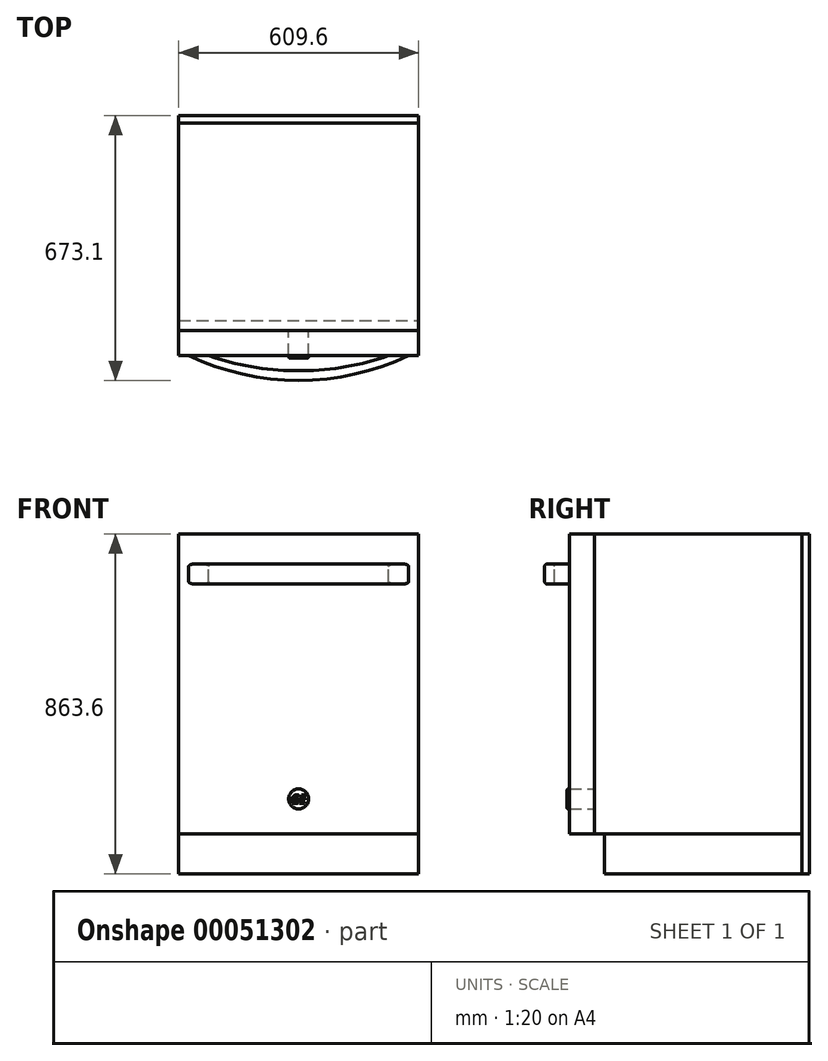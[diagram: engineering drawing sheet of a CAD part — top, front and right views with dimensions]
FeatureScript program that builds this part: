
annotation { "Feature Type Name" : "Feature", "Feature Type Description" : "" }
export const myFeature = defineFeature(function(context is Context, id is Id, definition is map)
    precondition{}
    {
        {
            var Q0;
            Q0=qCreatedBy(makeId("Front.planeOp"),FACE);
            var sketch = newSketch(context, id + "F0", { "sketchPlane" : qUnion([Q0])});
            skLineSegment(sketch, "E0.bottom", {"start": v(-304.8, 431.8) * mm, "end": v(304.8, 431.8) * mm});
            skLineSegment(sketch, "E0.top", {"start": v(-304.8, -431.8) * mm, "end": v(304.8, -431.8) * mm});
            skLineSegment(sketch, "E0.left", {"start": v(-304.8, 431.8) * mm, "end": v(-304.8, -431.8) * mm});
            skLineSegment(sketch, "E0.right", {"start": v(304.8, 431.8) * mm, "end": v(304.8, -431.8) * mm});
            skLineSegment(sketch, "E1", {"start": v(-304.8, 431.8) * mm, "end": v(304.8, -431.8) * mm, "construction": true});
            skLineSegment(sketch, "E2.bottom", {"start": v(-304.8, -330.2) * mm, "end": v(304.8, -330.2) * mm});
            skLineSegment(sketch, "E2.left", {"start": v(-304.8, -330.2) * mm, "end": v(-304.8, 431.8) * mm});
            skLineSegment(sketch, "E2.right", {"start": v(304.8, -330.2) * mm, "end": v(304.8, 431.8) * mm});
            skLineSegment(sketch, "E3", {"start": v(0, 0) * mm, "end": v(0, -330.2) * mm, "construction": true});
            skCircle(sketch, "E4", {"center": v(0, -241.3) * mm, "radius": 25.4 * mm});
            skLineSegment(sketch, "E5.bottom", {"start": v(-279.4, 355.6) * mm, "end": v(279.4, 355.6) * mm});
            skLineSegment(sketch, "E5.top", {"start": v(-279.4, 304.8) * mm, "end": v(279.4, 304.8) * mm});
            skLineSegment(sketch, "E5.left", {"start": v(-279.4, 355.6) * mm, "end": v(-279.4, 304.8) * mm});
            skLineSegment(sketch, "E5.right", {"start": v(279.4, 355.6) * mm, "end": v(279.4, 304.8) * mm});
            skLineSegment(sketch, "E6", {"start": v(0, 431.8) * mm, "end": v(0, 304.8) * mm, "construction": true});
            skSolve(sketch);
        }
        {
            var Q0;
            Q0=makeQuery(id+"F0.imprint","IMPRINT",FACE,{"disambiguationData":[TD([[makeQuery(id+"F0.imprint","IMPRINT",EDGE,{"derivedFrom":sQuery(id+"F0.wireOp",EDGE,"E2.bottom")}),1.0]])]});
            var Q1;
            Q1=makeQuery(id+"F0.imprint","IMPRINT",FACE,{"disambiguationData":[TD([[makeQuery(id+"F0.imprint","IMPRINT",EDGE,{"derivedFrom":sQuery(id+"F0.wireOp",EDGE,"E5.bottom")}),-1.0]])]});
            var Q2;
            Q2=makeQuery(id+"F0.imprint","IMPRINT",FACE,{"disambiguationData":[TD([[makeQuery(id+"F0.imprint","IMPRINT",EDGE,{"derivedFrom":sQuery(id+"F0.wireOp",EDGE,"E4")}),1.0]])]});
            var Q3;
            Q3=sQuery(id+"F0.wireOp",EDGE,"E2.right");
            var Q4;
            Q4=sQuery(id+"F0.wireOp",EDGE,"E0.bottom");
            var Q5;
            Q5=sQuery(id+"F0.wireOp",EDGE,"E2.left");
            var Q6;
            Q6=sQuery(id+"F0.wireOp",EDGE,"E2.bottom");
            extrude(context, id + "F1", {"entities" : qUnion([Q0, Q1, Q2]), "surfaceEntities" : qUnion([Q3, Q4, Q5, Q6]), "depth" : 63.5 * mm});
        }
        {
            var Q0;
            Q0=makeQuery(id+"F0.imprint","IMPRINT",FACE,{"disambiguationData":[TD([[makeQuery(id+"F0.imprint","IMPRINT",EDGE,{"derivedFrom":sQuery(id+"F0.wireOp",EDGE,"E0.top")}),1.0]])]});
            extrude(context, id + "F2", {"entities" : qUnion([Q0]), "oppositeDirection" : true, "depth" : 527.05 * mm});
        }
        {
            var Q0;
            Q0=makeQuery(id+"F0.imprint","IMPRINT",FACE,{"disambiguationData":[TD([[makeQuery(id+"F0.imprint","IMPRINT",EDGE,{"derivedFrom":sQuery(id+"F0.wireOp",EDGE,"E5.bottom")}),-1.0]])]});
            extrude(context, id + "F3", {"entities" : qUnion([Q0]), "operationType" : NewBodyOperationType.ADD, "depth" : 127 * mm});
        }
        {
            var Q0;
            Q0=makeQuery(id+"F3.opExtrude","SWEPT_FACE",FACE,{"disambiguationData":[OSD([sQuery(id+"F0.wireOp",EDGE,"E5.bottom")])]});
            var sketch = newSketch(context, id + "F4", { "sketchPlane" : qUnion([Q0])});
            skLineSegment(sketch, "E7.bottom", {"start": v(-228.6, -63.5) * mm, "end": v(228.6, -63.5) * mm});
            skLineSegment(sketch, "E7.top", {"start": v(-228.6, -101.6) * mm, "end": v(228.6, -101.6) * mm});
            skLineSegment(sketch, "E7.left", {"start": v(-228.6, -63.5) * mm, "end": v(-228.6, -101.6) * mm});
            skLineSegment(sketch, "E7.right", {"start": v(228.6, -63.5) * mm, "end": v(228.6, -101.6) * mm});
            skSolve(sketch);
        }
        {
            var Q0;
            Q0=qSketchRegion(id+"F4",true);
            extrude(context, id + "F5", {"entities" : qUnion([Q0]), "operationType" : NewBodyOperationType.REMOVE, "endBound" : BoundingType.THROUGH_ALL, "oppositeDirection" : true, "depth" : 25.4 * mm});
        }
        {
            var Q0;
            Q0=makeQuery(id+"F5.boolean.opBoolean","COPY",EDGE,{"derivedFrom":makeQuery(id+"F5.opExtrude","SWEPT_EDGE",EDGE,{"disambiguationData":[OSD([sQuery(id+"F4.wireOp",EDGE,"E7.top"),sQuery(id+"F4.wireOp",EDGE,"E7.right")])]})});
            var Q1;
            Q1=makeQuery(id+"F5.boolean.opBoolean","COPY",EDGE,{"derivedFrom":makeQuery(id+"F5.opExtrude","SWEPT_EDGE",EDGE,{"disambiguationData":[OSD([sQuery(id+"F4.wireOp",EDGE,"E7.top"),sQuery(id+"F4.wireOp",EDGE,"E7.left")])]})});
            var Q2;
            Q2=makeQuery(id+"F3.opExtrude","CAP_EDGE",EDGE,{"disambiguationData":[OSD([sQuery(id+"F0.wireOp",EDGE,"E5.left")])],"isStart":false});
            var Q3;
            Q3=makeQuery(id+"F3.opExtrude","CAP_EDGE",EDGE,{"disambiguationData":[OSD([sQuery(id+"F0.wireOp",EDGE,"E5.right")])],"isStart":false});
            fillet(context, id + "F6", {"entities" : qUnion([Q0, Q1, Q2, Q3]), "radius" : 646.43 * mm, "tangentPropagation" : true, "allowEdgeOverflow" : false});
        }
        {
            var Q0;
            Q0=makeQuery(id+"F6.opFillet","BLEND_EDGE",EDGE,{"blendedFrom":[makeQuery(id+"F3.opExtrude","CAP_EDGE",EDGE,{"disambiguationData":[OSD([sQuery(id+"F0.wireOp",EDGE,"E5.left")])],"isStart":false}),makeQuery(id+"F3.opExtrude","SWEPT_FACE",FACE,{"disambiguationData":[OSD([sQuery(id+"F0.wireOp",EDGE,"E5.bottom")])]})],"blendedInto":[makeQuery(id+"F3.opExtrude","SWEPT_FACE",FACE,{"disambiguationData":[OSD([sQuery(id+"F0.wireOp",EDGE,"E5.bottom")])]})]});
            var Q1;
            Q1=makeQuery(id+"F6.opFillet","BLEND_EDGE",EDGE,{"blendedFrom":[makeQuery(id+"F5.boolean.opBoolean","COPY",EDGE,{"derivedFrom":makeQuery(id+"F5.opExtrude","SWEPT_EDGE",EDGE,{"disambiguationData":[OSD([sQuery(id+"F4.wireOp",EDGE,"E7.top"),sQuery(id+"F4.wireOp",EDGE,"E7.right")])]})}),makeQuery(id+"F3.opExtrude","SWEPT_FACE",FACE,{"disambiguationData":[OSD([sQuery(id+"F0.wireOp",EDGE,"E5.bottom")])]})],"blendedInto":[makeQuery(id+"F3.opExtrude","SWEPT_FACE",FACE,{"disambiguationData":[OSD([sQuery(id+"F0.wireOp",EDGE,"E5.bottom")])]})]});
            var Q2;
            Q2=makeQuery(id+"F6.opFillet","BLEND_EDGE",EDGE,{"blendedFrom":[makeQuery(id+"F5.boolean.opBoolean","COPY",EDGE,{"derivedFrom":makeQuery(id+"F5.opExtrude","SWEPT_EDGE",EDGE,{"disambiguationData":[OSD([sQuery(id+"F4.wireOp",EDGE,"E7.top"),sQuery(id+"F4.wireOp",EDGE,"E7.left")])]})}),makeQuery(id+"F3.opExtrude","SWEPT_FACE",FACE,{"disambiguationData":[OSD([sQuery(id+"F0.wireOp",EDGE,"E5.bottom")])]})],"blendedInto":[makeQuery(id+"F3.opExtrude","SWEPT_FACE",FACE,{"disambiguationData":[OSD([sQuery(id+"F0.wireOp",EDGE,"E5.bottom")])]})]});
            var Q3;
            Q3=makeQuery(id+"F5.boolean.opBoolean","COPY",EDGE,{"derivedFrom":makeQuery(id+"F5.opExtrude","CAP_EDGE",EDGE,{"disambiguationData":[OSD([sQuery(id+"F4.wireOp",EDGE,"E7.top")])],"isStart":true})});
            var Q4;
            Q4=makeQuery(id+"F6.opFillet","BLEND_EDGE",EDGE,{"blendedFrom":[makeQuery(id+"F3.opExtrude","CAP_EDGE",EDGE,{"disambiguationData":[OSD([sQuery(id+"F0.wireOp",EDGE,"E5.right")])],"isStart":false}),makeQuery(id+"F3.opExtrude","SWEPT_FACE",FACE,{"disambiguationData":[OSD([sQuery(id+"F0.wireOp",EDGE,"E5.bottom")])]})],"blendedInto":[makeQuery(id+"F3.opExtrude","SWEPT_FACE",FACE,{"disambiguationData":[OSD([sQuery(id+"F0.wireOp",EDGE,"E5.bottom")])]})]});
            var Q5;
            Q5=makeQuery(id+"F6.opFillet","BLEND_EDGE",EDGE,{"blendedFrom":[makeQuery(id+"F3.opExtrude","CAP_EDGE",EDGE,{"disambiguationData":[OSD([sQuery(id+"F0.wireOp",EDGE,"E5.right")])],"isStart":false}),makeQuery(id+"F3.opExtrude","SWEPT_FACE",FACE,{"disambiguationData":[OSD([sQuery(id+"F0.wireOp",EDGE,"E5.top")])]})],"blendedInto":[makeQuery(id+"F3.opExtrude","SWEPT_FACE",FACE,{"disambiguationData":[OSD([sQuery(id+"F0.wireOp",EDGE,"E5.top")])]})]});
            var Q6;
            Q6=makeQuery(id+"F6.opFillet","BLEND_EDGE",EDGE,{"blendedFrom":[makeQuery(id+"F3.opExtrude","CAP_EDGE",EDGE,{"disambiguationData":[OSD([sQuery(id+"F0.wireOp",EDGE,"E5.left")])],"isStart":false}),makeQuery(id+"F3.opExtrude","SWEPT_FACE",FACE,{"disambiguationData":[OSD([sQuery(id+"F0.wireOp",EDGE,"E5.top")])]})],"blendedInto":[makeQuery(id+"F3.opExtrude","SWEPT_FACE",FACE,{"disambiguationData":[OSD([sQuery(id+"F0.wireOp",EDGE,"E5.top")])]})]});
            var Q7;
            Q7=makeQuery(id+"F6.opFillet","BLEND_EDGE",EDGE,{"blendedFrom":[makeQuery(id+"F5.boolean.opBoolean","COPY",EDGE,{"derivedFrom":makeQuery(id+"F5.opExtrude","SWEPT_EDGE",EDGE,{"disambiguationData":[OSD([sQuery(id+"F4.wireOp",EDGE,"E7.top"),sQuery(id+"F4.wireOp",EDGE,"E7.left")])]})}),makeQuery(id+"F3.opExtrude","SWEPT_FACE",FACE,{"disambiguationData":[OSD([sQuery(id+"F0.wireOp",EDGE,"E5.top")])]})],"blendedInto":[makeQuery(id+"F3.opExtrude","SWEPT_FACE",FACE,{"disambiguationData":[OSD([sQuery(id+"F0.wireOp",EDGE,"E5.top")])]})]});
            var Q8;
            Q8=makeQuery(id+"F6.opFillet","BLEND_EDGE",EDGE,{"blendedFrom":[makeQuery(id+"F5.boolean.opBoolean","COPY",EDGE,{"derivedFrom":makeQuery(id+"F5.opExtrude","SWEPT_EDGE",EDGE,{"disambiguationData":[OSD([sQuery(id+"F4.wireOp",EDGE,"E7.top"),sQuery(id+"F4.wireOp",EDGE,"E7.right")])]})}),makeQuery(id+"F3.opExtrude","SWEPT_FACE",FACE,{"disambiguationData":[OSD([sQuery(id+"F0.wireOp",EDGE,"E5.top")])]})],"blendedInto":[makeQuery(id+"F3.opExtrude","SWEPT_FACE",FACE,{"disambiguationData":[OSD([sQuery(id+"F0.wireOp",EDGE,"E5.top")])]})]});
            var Q9;
            Q9=makeQuery(id+"F5.boolean.opBoolean","INTERSECT",EDGE,{"derivedFrom":[makeQuery(id+"F3.opExtrude","SWEPT_FACE",FACE,{"disambiguationData":[OSD([sQuery(id+"F0.wireOp",EDGE,"E5.top")])]}),makeQuery(id+"F5.opExtrude","SWEPT_FACE",FACE,{"disambiguationData":[OSD([sQuery(id+"F4.wireOp",EDGE,"E7.top")])]})]});
            fillet(context, id + "F7", {"entities" : qUnion([Q0, Q1, Q2, Q3, Q4, Q5, Q6, Q7, Q8, Q9]), "radius" : 6.35 * mm, "tangentPropagation" : true, "allowEdgeOverflow" : false});
        }
        {
            var Q0;
            Q0=makeQuery(id+"F1.opExtrude","CAP_FACE",FACE,{"disambiguationData":[OSD([sQuery(id+"F0.wireOp",EDGE,"E2.bottom"),sQuery(id+"F0.wireOp",EDGE,"E0.bottom"),sQuery(id+"F0.wireOp",EDGE,"E2.left"),sQuery(id+"F0.wireOp",EDGE,"E2.right")])],"isStart":true});
            var Q1;
            Q1=makeQuery(id+"F2.opExtrude","CAP_FACE",FACE,{"disambiguationData":[OSD([sQuery(id+"F0.wireOp",EDGE,"E0.top"),sQuery(id+"F0.wireOp",EDGE,"E0.left"),sQuery(id+"F0.wireOp",EDGE,"E0.right"),sQuery(id+"F0.wireOp",EDGE,"E2.bottom")])],"isStart":false});
            extrude(context, id + "F8", {"entities" : qUnion([Q0]), "endBound" : BoundingType.UP_TO_SURFACE, "endBoundEntityFace" : qUnion([Q1]), "depth" : 25.4 * mm});
        }
        {
            var Q0;
            Q0=makeQuery(id+"F1.opExtrude","SWEPT_EDGE",EDGE,{"disambiguationData":[OSD([sQuery(id+"F0.wireOp",EDGE,"E0.left"),sQuery(id+"F0.wireOp",EDGE,"E2.bottom"),sQuery(id+"F0.wireOp",EDGE,"E2.left")])]});
            var Q1;
            Q1=makeQuery(id+"F1.opExtrude","SWEPT_EDGE",EDGE,{"disambiguationData":[OSD([sQuery(id+"F0.wireOp",EDGE,"E0.right"),sQuery(id+"F0.wireOp",EDGE,"E2.bottom"),sQuery(id+"F0.wireOp",EDGE,"E2.right")])]});
            fillet(context, id + "F9", {"entities" : qUnion([Q0, Q1]), "radius" : 6.35 * mm, "tangentPropagation" : true, "allowEdgeOverflow" : false});
        }
        {
            var Q0;
            Q0=makeQuery(id+"F0.imprint","IMPRINT",FACE,{"disambiguationData":[TD([[makeQuery(id+"F0.imprint","IMPRINT",EDGE,{"derivedFrom":sQuery(id+"F0.wireOp",EDGE,"E4")}),1.0]])]});
            var Q1;
            Q1=sQuery(id+"F0.wireOp",EDGE,"E4");
            extrude(context, id + "F10", {"entities" : qUnion([Q0]), "surfaceEntities" : qUnion([Q1]), "depth" : 69.85 * mm});
        }
        {
            var Q0;
            Q0=makeQuery(id+"F10.opExtrude","CAP_EDGE",EDGE,{"disambiguationData":[OSD([sQuery(id+"F0.wireOp",EDGE,"E4")])],"isStart":false});
            fillet(context, id + "F11", {"entities" : qUnion([Q0]), "radius" : 3.17 * mm, "tangentPropagation" : true, "allowEdgeOverflow" : false});
        }
        {
            var Q0;
            Q0=makeQuery(id+"F10.opExtrude","CAP_FACE",FACE,{"disambiguationData":[OSD([sQuery(id+"F0.wireOp",EDGE,"E4")])],"isStart":false});
            var sketch = newSketch(context, id + "F12", { "sketchPlane" : qUnion([Q0])});
            skText(sketch, "E8", { "text": "GE", "fontName": "OpenSans-BoldItalic.ttf"});
            const initialGuessF12  = {"E8": [-0.0191, -0.25284, 1, 0, 0.02166]};
            skSetInitialGuess(sketch, initialGuessF12);
            skSolve(sketch);
        }
        {
            var Q0;
            Q0=qSketchRegion(id+"F12",true);
            extrude(context, id + "F13", {"entities" : qUnion([Q0]), "operationType" : NewBodyOperationType.REMOVE, "oppositeDirection" : true, "depth" : 3.17 * mm});
        }
        {
            var Q0;
            Q0=makeQuery(id+"F2.opExtrude","CAP_FACE",FACE,{"disambiguationData":[OSD([sQuery(id+"F0.wireOp",EDGE,"E0.top"),sQuery(id+"F0.wireOp",EDGE,"E0.left"),sQuery(id+"F0.wireOp",EDGE,"E0.right"),sQuery(id+"F0.wireOp",EDGE,"E2.bottom")])],"isStart":true});
            extrude(context, id + "F14", {"entities" : qUnion([Q0]), "operationType" : NewBodyOperationType.REMOVE, "oppositeDirection" : true, "depth" : 25.4 * mm});
        }
        {
            var Q0;
            Q0=makeQuery(id+"F8.opExtrude","CAP_FACE",FACE,{"disambiguationData":[OSD([sQuery(id+"F0.wireOp",EDGE,"E2.bottom"),sQuery(id+"F0.wireOp",EDGE,"E0.bottom"),sQuery(id+"F0.wireOp",EDGE,"E2.left"),sQuery(id+"F0.wireOp",EDGE,"E2.right")])],"isStart":false});
            var sketch = newSketch(context, id + "F15", { "sketchPlane" : qUnion([Q0])});
            skLineSegment(sketch, "E9.bottom", {"start": v(304.8, 431.8) * mm, "end": v(-304.8, 431.8) * mm});
            skLineSegment(sketch, "E9.top", {"start": v(304.8, -431.8) * mm, "end": v(-304.8, -431.8) * mm});
            skLineSegment(sketch, "E9.left", {"start": v(304.8, 431.8) * mm, "end": v(304.8, -431.8) * mm});
            skLineSegment(sketch, "E9.right", {"start": v(-304.8, 431.8) * mm, "end": v(-304.8, -431.8) * mm});
            skSolve(sketch);
        }
        {
            var Q0;
            Q0=qSketchRegion(id+"F15",true);
            extrude(context, id + "F16", {"entities" : qUnion([Q0]), "depth" : 19.05 * mm});
        }
    });
